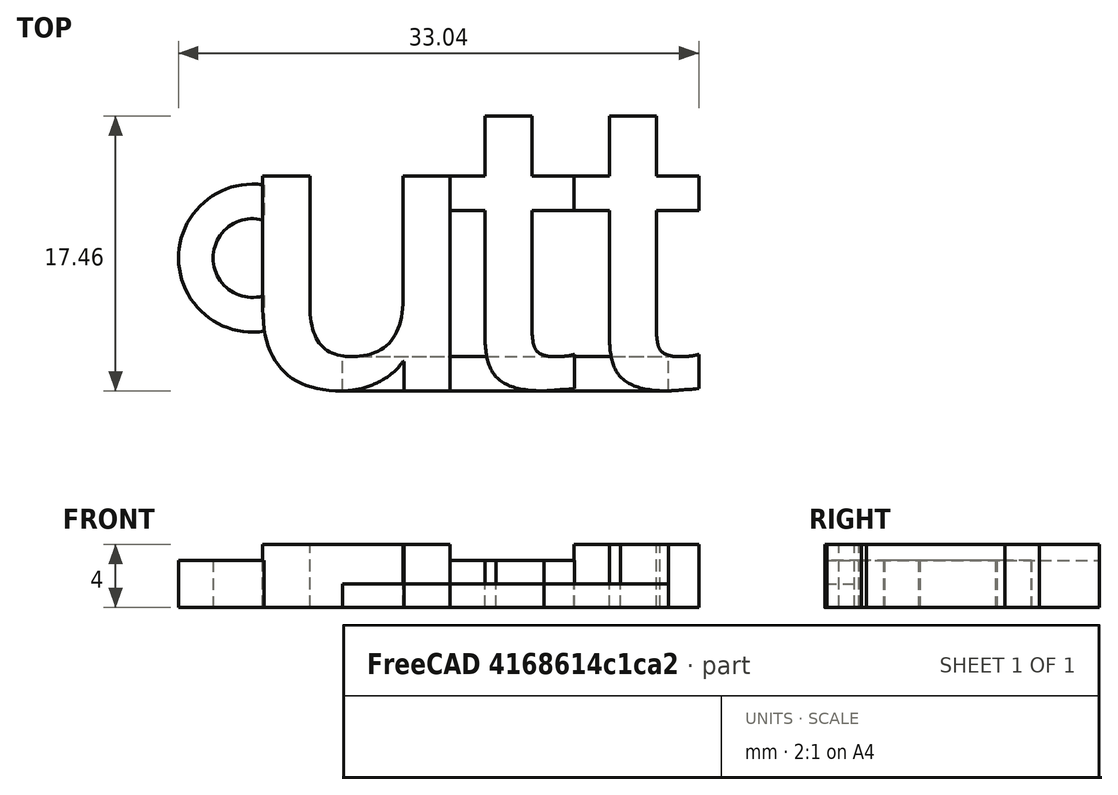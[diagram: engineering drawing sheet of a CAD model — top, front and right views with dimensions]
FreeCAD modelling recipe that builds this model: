
FCSTD DOCUMENT  (FreeCAD 0.18.4R)
Label: UTTporteCle
License: All rights reserved
LicenseURL: http://en.wikipedia.org/wiki/All_rights_reserved
objects: Part::Part2DObjectPython×6, Part::Extrusion×6, Part::Cut×2, Part::Box×1
note: 15 computed .brp shape members not serialized (recipe doc carries the construction recipe); baked Part::Feature solids carry a one-line shape summary decoded from their .brp

FEATURE [Part::Part2DObjectPython] ShapeString  # Draft 2D object (typed FeaturePython)
  FontFile = <userpath>/Documents/UTT/MindTech/Impression3D/HelveticaNeueMed.ttf
  Placement = pos=(-15.12,0,0) rot=(0,0,1;0rad)
  Size = 10
  String = u
  Tracking = 0
FEATURE [Part::Part2DObjectPython] ShapeString001  # Draft 2D object (typed FeaturePython)
  FontFile = <userpath>/Documents/UTT/MindTech/Impression3D/HelveticaNeueMed.ttf
  Placement = pos=(-3.1,0,0) rot=(0,0,1;0rad)
  Size = 10
  String = t
  Tracking = 0
FEATURE [Part::Part2DObjectPython] ShapeString002  # Draft 2D object (typed FeaturePython)
  FontFile = <userpath>/Documents/UTT/MindTech/Impression3D/HelveticaNeueMed.ttf
  Placement = pos=(8.5,0,0) rot=(0,0,1;0rad)
  Size = 10
  String = t
  Tracking = 0
FEATURE [Part::Part2DObjectPython] Circle001  # Draft 2D object (typed FeaturePython)
  FirstAngle = 0
  LastAngle = 0
  MakeFace = false
  Placement = pos=(-13,5.44,0) rot=(0,0,1;0rad)
  Radius = 4.7
FEATURE [Part::Part2DObjectPython] Circle  # Draft 2D object (typed FeaturePython)
  FirstAngle = 0
  LastAngle = 0
  MakeFace = false
  Placement = pos=(-13,5.44,0) rot=(0,0,1;0rad)
  Radius = 2.5
FEATURE [Part::Part2DObjectPython] Rectangle  # Draft 2D object (typed FeaturePython)
  ChamferSize = 0
  Columns = 1
  FilletRadius = 0
  Height = 14.8589
  Length = 6.79072
  MakeFace = false
  Placement = pos=(-12.2587,-1.93996,0) rot=(0,0,1;0rad)
  Rows = 1
FEATURE [Part::Extrusion] Extrude
  Base = -> ShapeString
  Dir = (0,0,1)
  DirMode = 2
  FaceMakerClass = Part::FaceMakerBullseye
  LengthFwd = 4
  LengthRev = 0
  Placement = pos=(-0.2,0,0) rot=(0,0,1;0rad)
  Solid = false
  Symmetric = false
FEATURE [Part::Extrusion] Extrude001
  Base = -> ShapeString001
  Dir = (0,0,1)
  DirMode = 2
  FaceMakerClass = Part::FaceMakerBullseye
  LengthFwd = 3
  LengthRev = 0
  Placement = pos=(1,0,0) rot=(0,0,1;0rad)
  Solid = false
  Symmetric = false
FEATURE [Part::Extrusion] Extrude002
  Base = -> ShapeString002
  Dir = (0,0,1)
  DirMode = 2
  FaceMakerClass = Part::FaceMakerBullseye
  LengthFwd = 4
  LengthRev = 0
  Placement = pos=(-2.7,0,0) rot=(0,0,1;0rad)
  Solid = false
  Symmetric = false
FEATURE [Part::Extrusion] Extrude003
  Base = -> Circle
  Dir = (0,0,1)
  DirMode = 2
  FaceMakerClass = Part::FaceMakerBullseye
  LengthFwd = 3
  LengthRev = 0
  Solid = true
  Symmetric = false
FEATURE [Part::Extrusion] Extrude004
  Base = -> Circle001
  Dir = (0,0,1)
  DirMode = 2
  FaceMakerClass = Part::FaceMakerBullseye
  LengthFwd = 3
  LengthRev = 0
  Solid = true
  Symmetric = false
FEATURE [Part::Extrusion] Extrude005
  Base = -> Rectangle
  Dir = (0,0,1)
  DirMode = 2
  FaceMakerClass = Part::FaceMakerBullseye
  LengthFwd = 3
  LengthRev = 0
  Solid = true
  Symmetric = false
FEATURE [Part::Cut] Cut
  Base = -> Extrude004
  Tool = -> Extrude003
FEATURE [Part::Cut] Cut001
  Base = -> Cut
  Placement = pos=(-1.4,3,0) rot=(0,0,1;0rad)
  Tool = -> Extrude005
FEATURE [Part::Box] Box  label="Cube"
  AttacherType = Attacher::AttachEngine3D
  Height = 1.5
  Length = 20.71
  Placement = pos=(-8.7,0,0) rot=(0,0,1;0rad)
  Width = 2.2
